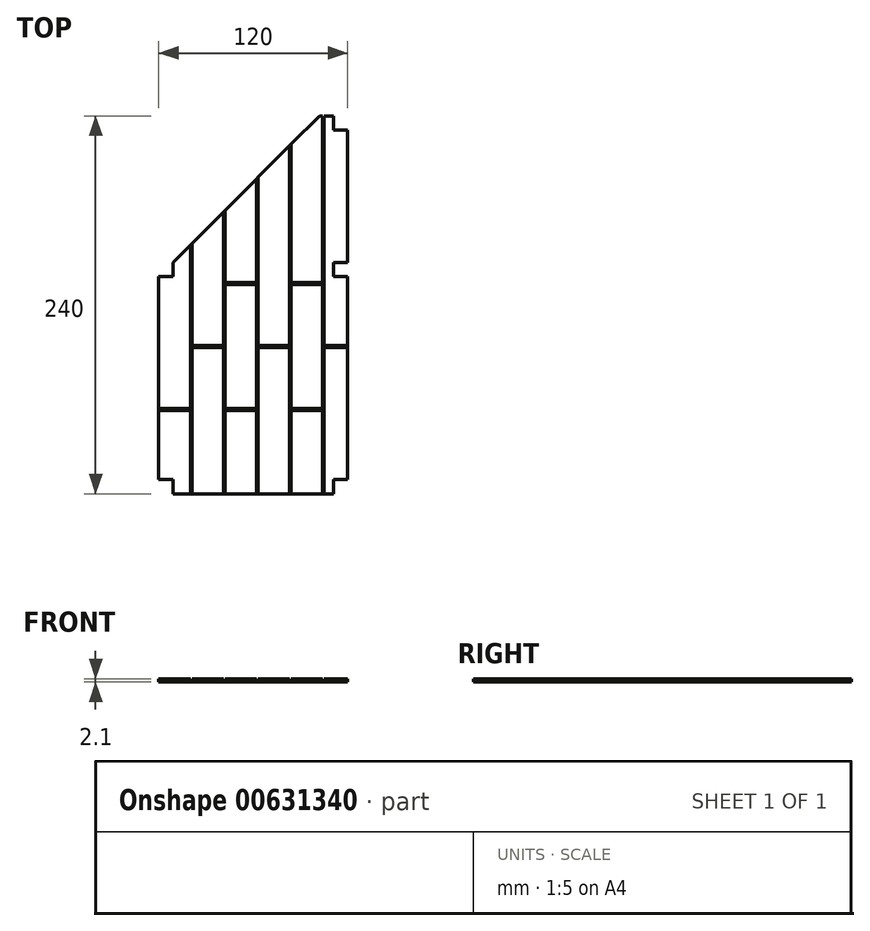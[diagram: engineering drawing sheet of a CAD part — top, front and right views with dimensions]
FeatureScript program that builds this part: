
annotation { "Feature Type Name" : "Feature", "Feature Type Description" : "" }
export const myFeature = defineFeature(function(context is Context, id is Id, definition is map)
    precondition{}
    {
        {
            var Q0;
            Q0=qCreatedBy(makeId("Top.planeOp"),FACE);
            var sketch = newSketch(context, id + "F0", { "sketchPlane" : qUnion([Q0])});
            skLineSegment(sketch, "E0.bottom", {"start": v(-143.47, 246.7) * mm, "end": v(-23.47, 246.7) * mm});
            skLineSegment(sketch, "E0.top", {"start": v(-143.47, 6.7) * mm, "end": v(-23.47, 6.7) * mm});
            skLineSegment(sketch, "E0.left", {"start": v(-143.47, 246.7) * mm, "end": v(-143.47, 6.7) * mm});
            skLineSegment(sketch, "E0.right", {"start": v(-23.47, 246.7) * mm, "end": v(-23.47, 6.7) * mm});
            skLineSegment(sketch, "E1.bottom", {"start": v(-143.47, 153.7) * mm, "end": v(-134.47, 153.7) * mm});
            skLineSegment(sketch, "E1.top", {"start": v(-143.47, 144.7) * mm, "end": v(-134.47, 144.7) * mm});
            skLineSegment(sketch, "E1.left", {"start": v(-143.47, 153.7) * mm, "end": v(-143.47, 144.7) * mm});
            skLineSegment(sketch, "E1.right", {"start": v(-134.47, 153.7) * mm, "end": v(-134.47, 144.7) * mm});
            skLineSegment(sketch, "E2.bottom", {"start": v(-134.47, 6.7) * mm, "end": v(-143.47, 6.7) * mm});
            skLineSegment(sketch, "E2.top", {"start": v(-134.47, 15.7) * mm, "end": v(-143.47, 15.7) * mm});
            skLineSegment(sketch, "E2.left", {"start": v(-134.47, 6.7) * mm, "end": v(-134.47, 15.7) * mm});
            skLineSegment(sketch, "E2.right", {"start": v(-143.47, 6.7) * mm, "end": v(-143.47, 15.7) * mm});
            skLineSegment(sketch, "E3.bottom", {"start": v(-23.47, 15.7) * mm, "end": v(-32.47, 15.7) * mm});
            skLineSegment(sketch, "E3.top", {"start": v(-23.47, 6.7) * mm, "end": v(-32.47, 6.7) * mm});
            skLineSegment(sketch, "E3.left", {"start": v(-23.47, 15.7) * mm, "end": v(-23.47, 6.7) * mm});
            skLineSegment(sketch, "E3.right", {"start": v(-32.47, 15.7) * mm, "end": v(-32.47, 6.7) * mm});
            skLineSegment(sketch, "E4.bottom", {"start": v(-23.47, 153.7) * mm, "end": v(-32.47, 153.7) * mm});
            skLineSegment(sketch, "E4.top", {"start": v(-23.47, 144.7) * mm, "end": v(-32.47, 144.7) * mm});
            skLineSegment(sketch, "E4.left", {"start": v(-23.47, 153.7) * mm, "end": v(-23.47, 144.7) * mm});
            skLineSegment(sketch, "E4.right", {"start": v(-32.47, 153.7) * mm, "end": v(-32.47, 144.7) * mm});
            skLineSegment(sketch, "E5.bottom", {"start": v(-23.47, 246.7) * mm, "end": v(-32.47, 246.7) * mm});
            skLineSegment(sketch, "E5.top", {"start": v(-23.47, 237.7) * mm, "end": v(-32.47, 237.7) * mm});
            skLineSegment(sketch, "E5.left", {"start": v(-23.47, 246.7) * mm, "end": v(-23.47, 237.7) * mm});
            skLineSegment(sketch, "E5.right", {"start": v(-32.47, 246.7) * mm, "end": v(-32.47, 237.7) * mm});
            skLineSegment(sketch, "E6.bottom", {"start": v(-32.47, 246.7) * mm, "end": v(-41.47, 246.7) * mm});
            skLineSegment(sketch, "E6.top", {"start": v(-32.47, 237.7) * mm, "end": v(-41.47, 237.7) * mm});
            skLineSegment(sketch, "E6.right", {"start": v(-41.47, 246.7) * mm, "end": v(-41.47, 237.7) * mm});
            skLineSegment(sketch, "E7", {"start": v(-41.47, 246.7) * mm, "end": v(-134.47, 153.7) * mm});
            skLineSegment(sketch, "E8", {"start": v(-123.47, 6.7) * mm, "end": v(-123.47, 164.7) * mm});
            skLineSegment(sketch, "E9", {"start": v(-122.47, 6.7) * mm, "end": v(-122.47, 165.7) * mm});
            skLineSegment(sketch, "E10", {"start": v(-102.47, 6.7) * mm, "end": v(-102.47, 185.7) * mm});
            skLineSegment(sketch, "E11", {"start": v(-101.47, 6.7) * mm, "end": v(-101.47, 186.7) * mm});
            skLineSegment(sketch, "E12", {"start": v(-81.47, 6.7) * mm, "end": v(-81.47, 206.7) * mm});
            skLineSegment(sketch, "E13", {"start": v(-80.47, 6.7) * mm, "end": v(-80.47, 207.7) * mm});
            skLineSegment(sketch, "E14", {"start": v(-60.47, 6.7) * mm, "end": v(-60.47, 227.7) * mm});
            skLineSegment(sketch, "E15", {"start": v(-59.47, 6.7) * mm, "end": v(-59.47, 228.7) * mm});
            skLineSegment(sketch, "E16", {"start": v(-39.47, 6.7) * mm, "end": v(-39.47, 246.7) * mm});
            skLineSegment(sketch, "E17", {"start": v(-143.47, 60.7) * mm, "end": v(-123.47, 60.7) * mm});
            skLineSegment(sketch, "E18", {"start": v(-143.47, 59.7) * mm, "end": v(-123.47, 59.7) * mm});
            skLineSegment(sketch, "E19", {"start": v(-122.47, 100.7) * mm, "end": v(-102.47, 100.7) * mm});
            skLineSegment(sketch, "E20", {"start": v(-122.47, 99.7) * mm, "end": v(-102.47, 99.7) * mm});
            skLineSegment(sketch, "E21.bottom", {"start": v(-143.47, 64.7) * mm, "end": v(-152.47, 64.7) * mm});
            skLineSegment(sketch, "E21.top", {"start": v(-143.47, 55.7) * mm, "end": v(-152.47, 55.7) * mm});
            skLineSegment(sketch, "E21.left", {"start": v(-143.47, 64.7) * mm, "end": v(-143.47, 55.7) * mm});
            skLineSegment(sketch, "E21.right", {"start": v(-152.47, 64.7) * mm, "end": v(-152.47, 55.7) * mm});
            skLineSegment(sketch, "E22.bottom", {"start": v(-143.47, 104.7) * mm, "end": v(-152.47, 104.7) * mm});
            skLineSegment(sketch, "E22.top", {"start": v(-143.47, 95.7) * mm, "end": v(-152.47, 95.7) * mm});
            skLineSegment(sketch, "E22.left", {"start": v(-143.47, 104.7) * mm, "end": v(-143.47, 95.7) * mm});
            skLineSegment(sketch, "E22.right", {"start": v(-152.47, 104.7) * mm, "end": v(-152.47, 95.7) * mm});
            skLineSegment(sketch, "E23", {"start": v(-101.47, 140.7) * mm, "end": v(-81.47, 140.7) * mm});
            skPoint(sketch, "E23.startSnap0", {"position": v(-134.47, 149.2) * mm});
            skLineSegment(sketch, "E24", {"start": v(-101.47, 139.7) * mm, "end": v(-81.47, 139.7) * mm});
            skLineSegment(sketch, "E25", {"start": v(-101.47, 60.7) * mm, "end": v(-81.47, 60.7) * mm});
            skLineSegment(sketch, "E26", {"start": v(-101.47, 59.7) * mm, "end": v(-81.47, 59.7) * mm});
            skLineSegment(sketch, "E27", {"start": v(-80.47, 100.7) * mm, "end": v(-60.47, 100.7) * mm});
            skLineSegment(sketch, "E28", {"start": v(-80.47, 99.7) * mm, "end": v(-60.47, 99.7) * mm});
            skLineSegment(sketch, "E29", {"start": v(-59.47, 140.7) * mm, "end": v(-39.47, 140.7) * mm});
            skLineSegment(sketch, "E30", {"start": v(-59.47, 139.7) * mm, "end": v(-39.47, 139.7) * mm});
            skLineSegment(sketch, "E31", {"start": v(-59.47, 60.7) * mm, "end": v(-39.47, 60.7) * mm});
            skLineSegment(sketch, "E32", {"start": v(-59.47, 59.7) * mm, "end": v(-39.47, 59.7) * mm});
            skLineSegment(sketch, "E33", {"start": v(-38.47, 246.7) * mm, "end": v(-38.47, 6.7) * mm});
            skLineSegment(sketch, "E34", {"start": v(-38.47, 100.7) * mm, "end": v(-23.47, 100.7) * mm});
            skLineSegment(sketch, "E35", {"start": v(-38.47, 99.7) * mm, "end": v(-23.47, 99.7) * mm});
            skSolve(sketch);
        }
        {
            var Q0;
            {var subQ4=sQuery(id+"F0.wireOp",EDGE,"E1.top");Q0=makeQuery(id+"F0.imprint","IMPRINT",FACE,{"disambiguationData":[TD([[makeQuery(id+"F0.imprint","IMPRINT",EDGE,{"derivedFrom":subQ4}),-1.0]])]});}
            var Q1;
            {var subQ0=sQuery(id+"F0.wireOp",EDGE,"iPl3nyO9-lugT-xWKg-2Qvq-ciyDfMvkzASw");Q1=makeQuery(id+"F0.imprint","IMPRINT",FACE,{"disambiguationData":[TD([[makeQuery(id+"F0.imprint","IMPRINT",EDGE,{"derivedFrom":subQ0}),-1.0]])]});}
            var Q2;
            {var subQ1=sQuery(id+"F0.wireOp",EDGE,"E2.top");Q2=makeQuery(id+"F0.imprint","IMPRINT",FACE,{"disambiguationData":[TD([[makeQuery(id+"F0.imprint","IMPRINT",EDGE,{"derivedFrom":subQ1}),-1.0]])]});}
            var Q3;
            {var subQ5=sQuery(id+"F0.wireOp",EDGE,"E20");Q3=makeQuery(id+"F0.imprint","IMPRINT",FACE,{"disambiguationData":[TD([[makeQuery(id+"F0.imprint","IMPRINT",EDGE,{"derivedFrom":subQ5}),-1.0]])]});}
            var Q4;
            {var subQ5=sQuery(id+"F0.wireOp",EDGE,"E19");Q4=makeQuery(id+"F0.imprint","IMPRINT",FACE,{"disambiguationData":[TD([[makeQuery(id+"F0.imprint","IMPRINT",EDGE,{"derivedFrom":subQ5}),1.0]])]});}
            var Q5;
            {var subQ5=sQuery(id+"F0.wireOp",EDGE,"E23");Q5=makeQuery(id+"F0.imprint","IMPRINT",FACE,{"disambiguationData":[TD([[makeQuery(id+"F0.imprint","IMPRINT",EDGE,{"derivedFrom":subQ5}),1.0]])]});}
            var Q6;
            {var subQ0=sQuery(id+"F0.wireOp",EDGE,"E24");Q6=makeQuery(id+"F0.imprint","IMPRINT",FACE,{"disambiguationData":[TD([[makeQuery(id+"F0.imprint","IMPRINT",EDGE,{"derivedFrom":subQ0}),-1.0]])]});}
            var Q7;
            {var subQ5=sQuery(id+"F0.wireOp",EDGE,"E26");Q7=makeQuery(id+"F0.imprint","IMPRINT",FACE,{"disambiguationData":[TD([[makeQuery(id+"F0.imprint","IMPRINT",EDGE,{"derivedFrom":subQ5}),-1.0]])]});}
            var Q8;
            {var subQ5=sQuery(id+"F0.wireOp",EDGE,"E27");Q8=makeQuery(id+"F0.imprint","IMPRINT",FACE,{"disambiguationData":[TD([[makeQuery(id+"F0.imprint","IMPRINT",EDGE,{"derivedFrom":subQ5}),1.0]])]});}
            var Q9;
            {var subQ5=sQuery(id+"F0.wireOp",EDGE,"E28");Q9=makeQuery(id+"F0.imprint","IMPRINT",FACE,{"disambiguationData":[TD([[makeQuery(id+"F0.imprint","IMPRINT",EDGE,{"derivedFrom":subQ5}),-1.0]])]});}
            var Q10;
            {var subQ4=sQuery(id+"F0.wireOp",EDGE,"E6.right");Q10=makeQuery(id+"F0.imprint","IMPRINT",FACE,{"disambiguationData":[TD([[makeQuery(id+"F0.imprint","IMPRINT",EDGE,{"derivedFrom":subQ4}),-1.0]])]});}
            var Q11;
            {var subQ0=sQuery(id+"F0.wireOp",EDGE,"E30");Q11=makeQuery(id+"F0.imprint","IMPRINT",FACE,{"disambiguationData":[TD([[makeQuery(id+"F0.imprint","IMPRINT",EDGE,{"derivedFrom":subQ0}),-1.0]])]});}
            var Q12;
            {var subQ5=sQuery(id+"F0.wireOp",EDGE,"E32");Q12=makeQuery(id+"F0.imprint","IMPRINT",FACE,{"disambiguationData":[TD([[makeQuery(id+"F0.imprint","IMPRINT",EDGE,{"derivedFrom":subQ5}),-1.0]])]});}
            var Q13;
            {var subQ0=sQuery(id+"F0.wireOp",EDGE,"E17");Q13=makeQuery(id+"F0.imprint","IMPRINT",FACE,{"disambiguationData":[TD([[makeQuery(id+"F0.imprint","IMPRINT",EDGE,{"derivedFrom":subQ0}),-1.0]])]});}
            var Q14;
            {var subQ0=sQuery(id+"F0.wireOp",EDGE,"E8");var subQ3=sQuery(id+"F0.wireOp",EDGE,"E0.top");var subQ4=makeQuery(id+"F0.imprint","INTERSECT",VERTEX,{"derivedFrom":[subQ3,subQ0]});Q14=makeQuery(id+"F0.imprint","IMPRINT",FACE,{"disambiguationData":[TD([[makeQuery(id+"F0.imprint","IMPRINT",EDGE,{"disambiguationData":[TD([[subQ4,-1.0]])],"derivedFrom":subQ3}),1.0]])]});}
            var Q15;
            {var subQ0=sQuery(id+"F0.wireOp",EDGE,"E19");Q15=makeQuery(id+"F0.imprint","IMPRINT",FACE,{"disambiguationData":[TD([[makeQuery(id+"F0.imprint","IMPRINT",EDGE,{"derivedFrom":subQ0}),-1.0]])]});}
            var Q16;
            {var subQ0=sQuery(id+"F0.wireOp",EDGE,"E10");var subQ7=sQuery(id+"F0.wireOp",EDGE,"E0.top");var subQ8=makeQuery(id+"F0.imprint","INTERSECT",VERTEX,{"derivedFrom":[subQ7,subQ0]});Q16=makeQuery(id+"F0.imprint","IMPRINT",FACE,{"disambiguationData":[TD([[makeQuery(id+"F0.imprint","IMPRINT",EDGE,{"disambiguationData":[TD([[subQ8,-1.0]])],"derivedFrom":subQ7}),1.0]])]});}
            var Q17;
            {var subQ0=sQuery(id+"F0.wireOp",EDGE,"E23");Q17=makeQuery(id+"F0.imprint","IMPRINT",FACE,{"disambiguationData":[TD([[makeQuery(id+"F0.imprint","IMPRINT",EDGE,{"derivedFrom":subQ0}),-1.0]])]});}
            var Q18;
            {var subQ0=sQuery(id+"F0.wireOp",EDGE,"E12");var subQ3=sQuery(id+"F0.wireOp",EDGE,"E0.top");var subQ4=makeQuery(id+"F0.imprint","INTERSECT",VERTEX,{"derivedFrom":[subQ3,subQ0]});Q18=makeQuery(id+"F0.imprint","IMPRINT",FACE,{"disambiguationData":[TD([[makeQuery(id+"F0.imprint","IMPRINT",EDGE,{"disambiguationData":[TD([[subQ4,-1.0]])],"derivedFrom":subQ3}),1.0]])]});}
            var Q19;
            {var subQ0=sQuery(id+"F0.wireOp",EDGE,"E27");Q19=makeQuery(id+"F0.imprint","IMPRINT",FACE,{"disambiguationData":[TD([[makeQuery(id+"F0.imprint","IMPRINT",EDGE,{"derivedFrom":subQ0}),-1.0]])]});}
            var Q20;
            {var subQ0=sQuery(id+"F0.wireOp",EDGE,"E14");var subQ1=sQuery(id+"F0.wireOp",EDGE,"E0.top");var subQ2=makeQuery(id+"F0.imprint","INTERSECT",VERTEX,{"derivedFrom":[subQ1,subQ0]});Q20=makeQuery(id+"F0.imprint","IMPRINT",FACE,{"disambiguationData":[TD([[makeQuery(id+"F0.imprint","IMPRINT",EDGE,{"disambiguationData":[TD([[subQ2,-1.0]])],"derivedFrom":subQ1}),1.0]])]});}
            var Q21;
            {var subQ0=sQuery(id+"F0.wireOp",EDGE,"E31");Q21=makeQuery(id+"F0.imprint","IMPRINT",FACE,{"disambiguationData":[TD([[makeQuery(id+"F0.imprint","IMPRINT",EDGE,{"derivedFrom":subQ0}),-1.0]])]});}
            var Q22;
            {var subQ0=sQuery(id+"F0.wireOp",EDGE,"E29");Q22=makeQuery(id+"F0.imprint","IMPRINT",FACE,{"disambiguationData":[TD([[makeQuery(id+"F0.imprint","IMPRINT",EDGE,{"derivedFrom":subQ0}),-1.0]])]});}
            var Q23;
            {var subQ0=sQuery(id+"F0.wireOp",EDGE,"E25");Q23=makeQuery(id+"F0.imprint","IMPRINT",FACE,{"disambiguationData":[TD([[makeQuery(id+"F0.imprint","IMPRINT",EDGE,{"derivedFrom":subQ0}),-1.0]])]});}
            var Q24;
            {var subQ5=sQuery(id+"F0.wireOp",EDGE,"E33");Q24=makeQuery(id+"F0.imprint","IMPRINT",FACE,{"disambiguationData":[TD([[makeQuery(id+"F0.imprint","IMPRINT",EDGE,{"derivedFrom":subQ5}),-1.0]])]});}
            var Q25;
            {var subQ9=sQuery(id+"F0.wireOp",EDGE,"E3.bottom");Q25=makeQuery(id+"F0.imprint","IMPRINT",FACE,{"disambiguationData":[TD([[makeQuery(id+"F0.imprint","IMPRINT",EDGE,{"derivedFrom":subQ9}),-1.0]])]});}
            var Q26;
            {var subQ1=sQuery(id+"F0.wireOp",EDGE,"E4.bottom");Q26=makeQuery(id+"F0.imprint","IMPRINT",FACE,{"disambiguationData":[TD([[makeQuery(id+"F0.imprint","IMPRINT",EDGE,{"derivedFrom":subQ1}),-1.0]])]});}
            var Q27;
            {var subQ0=sQuery(id+"F0.wireOp",EDGE,"E34");Q27=makeQuery(id+"F0.imprint","IMPRINT",FACE,{"disambiguationData":[TD([[makeQuery(id+"F0.imprint","IMPRINT",EDGE,{"derivedFrom":subQ0}),-1.0]])]});}
            var Q28;
            {var subQ0=sQuery(id+"F0.wireOp",EDGE,"E6.right");Q28=makeQuery(id+"F0.imprint","IMPRINT",FACE,{"disambiguationData":[TD([[makeQuery(id+"F0.imprint","IMPRINT",EDGE,{"derivedFrom":subQ0}),1.0]])]});}
            var Q29;
            {var subQ0=sQuery(id+"F0.wireOp",EDGE,"E16");var subQ1=sQuery(id+"F0.wireOp",EDGE,"E6.bottom");var subQ2=makeQuery(id+"F0.imprint","INTERSECT",VERTEX,{"derivedFrom":[subQ1,subQ0]});Q29=makeQuery(id+"F0.imprint","IMPRINT",FACE,{"disambiguationData":[TD([[makeQuery(id+"F0.imprint","IMPRINT",EDGE,{"disambiguationData":[TD([[subQ2,1.0]])],"derivedFrom":subQ1}),1.0]])]});}
            var Q30;
            {var subQ0=sQuery(id+"F0.wireOp",EDGE,"E5.right");Q30=makeQuery(id+"F0.imprint","IMPRINT",FACE,{"disambiguationData":[TD([[makeQuery(id+"F0.imprint","IMPRINT",EDGE,{"derivedFrom":subQ0}),-1.0]])]});}
            extrude(context, id + "F1", {"entities" : qUnion([Q0, Q1, Q2, Q3, Q4, Q5, Q6, Q7, Q8, Q9, Q10, Q11, Q12, Q13, Q14, Q15, Q16, Q17, Q18, Q19, Q20, Q21, Q22, Q23, Q24, Q25, Q26, Q27, Q28, Q29, Q30]), "depth" : -0.1 * mm, "offsetDistance" : 25 * mm});
        }
        {
            var Q0;
            {var subQ2=sQuery(id+"F0.wireOp",EDGE,"E1.top");Q0=makeQuery(id+"F0.imprint","IMPRINT",FACE,{"disambiguationData":[TD([[makeQuery(id+"F0.imprint","IMPRINT",EDGE,{"derivedFrom":subQ2}),-1.0]])]});}
            var Q1;
            {var subQ4=sQuery(id+"F0.wireOp",EDGE,"E2.top");Q1=makeQuery(id+"F0.imprint","IMPRINT",FACE,{"disambiguationData":[TD([[makeQuery(id+"F0.imprint","IMPRINT",EDGE,{"derivedFrom":subQ4}),-1.0]])]});}
            var Q2;
            {var subQ5=sQuery(id+"F0.wireOp",EDGE,"E20");Q2=makeQuery(id+"F0.imprint","IMPRINT",FACE,{"disambiguationData":[TD([[makeQuery(id+"F0.imprint","IMPRINT",EDGE,{"derivedFrom":subQ5}),-1.0]])]});}
            var Q3;
            {var subQ5=sQuery(id+"F0.wireOp",EDGE,"E19");Q3=makeQuery(id+"F0.imprint","IMPRINT",FACE,{"disambiguationData":[TD([[makeQuery(id+"F0.imprint","IMPRINT",EDGE,{"derivedFrom":subQ5}),1.0]])]});}
            var Q4;
            {var subQ5=sQuery(id+"F0.wireOp",EDGE,"E23");Q4=makeQuery(id+"F0.imprint","IMPRINT",FACE,{"disambiguationData":[TD([[makeQuery(id+"F0.imprint","IMPRINT",EDGE,{"derivedFrom":subQ5}),1.0]])]});}
            var Q5;
            {var subQ0=sQuery(id+"F0.wireOp",EDGE,"E24");Q5=makeQuery(id+"F0.imprint","IMPRINT",FACE,{"disambiguationData":[TD([[makeQuery(id+"F0.imprint","IMPRINT",EDGE,{"derivedFrom":subQ0}),-1.0]])]});}
            var Q6;
            {var subQ5=sQuery(id+"F0.wireOp",EDGE,"E26");Q6=makeQuery(id+"F0.imprint","IMPRINT",FACE,{"disambiguationData":[TD([[makeQuery(id+"F0.imprint","IMPRINT",EDGE,{"derivedFrom":subQ5}),-1.0]])]});}
            var Q7;
            {var subQ5=sQuery(id+"F0.wireOp",EDGE,"E28");Q7=makeQuery(id+"F0.imprint","IMPRINT",FACE,{"disambiguationData":[TD([[makeQuery(id+"F0.imprint","IMPRINT",EDGE,{"derivedFrom":subQ5}),-1.0]])]});}
            var Q8;
            {var subQ5=sQuery(id+"F0.wireOp",EDGE,"E27");Q8=makeQuery(id+"F0.imprint","IMPRINT",FACE,{"disambiguationData":[TD([[makeQuery(id+"F0.imprint","IMPRINT",EDGE,{"derivedFrom":subQ5}),1.0]])]});}
            var Q9;
            {var subQ4=sQuery(id+"F0.wireOp",EDGE,"E6.right");Q9=makeQuery(id+"F0.imprint","IMPRINT",FACE,{"disambiguationData":[TD([[makeQuery(id+"F0.imprint","IMPRINT",EDGE,{"derivedFrom":subQ4}),-1.0]])]});}
            var Q10;
            {var subQ0=sQuery(id+"F0.wireOp",EDGE,"E30");Q10=makeQuery(id+"F0.imprint","IMPRINT",FACE,{"disambiguationData":[TD([[makeQuery(id+"F0.imprint","IMPRINT",EDGE,{"derivedFrom":subQ0}),-1.0]])]});}
            var Q11;
            {var subQ5=sQuery(id+"F0.wireOp",EDGE,"E32");Q11=makeQuery(id+"F0.imprint","IMPRINT",FACE,{"disambiguationData":[TD([[makeQuery(id+"F0.imprint","IMPRINT",EDGE,{"derivedFrom":subQ5}),-1.0]])]});}
            var Q12;
            {var subQ9=sQuery(id+"F0.wireOp",EDGE,"E3.bottom");Q12=makeQuery(id+"F0.imprint","IMPRINT",FACE,{"disambiguationData":[TD([[makeQuery(id+"F0.imprint","IMPRINT",EDGE,{"derivedFrom":subQ9}),-1.0]])]});}
            var Q13;
            {var subQ1=sQuery(id+"F0.wireOp",EDGE,"E4.bottom");Q13=makeQuery(id+"F0.imprint","IMPRINT",FACE,{"disambiguationData":[TD([[makeQuery(id+"F0.imprint","IMPRINT",EDGE,{"derivedFrom":subQ1}),-1.0]])]});}
            var Q14;
            {var subQ0=sQuery(id+"F0.wireOp",EDGE,"E6.right");Q14=makeQuery(id+"F0.imprint","IMPRINT",FACE,{"disambiguationData":[TD([[makeQuery(id+"F0.imprint","IMPRINT",EDGE,{"derivedFrom":subQ0}),1.0]])]});}
            var Q15;
            {var subQ0=sQuery(id+"F0.wireOp",EDGE,"E5.right");Q15=makeQuery(id+"F0.imprint","IMPRINT",FACE,{"disambiguationData":[TD([[makeQuery(id+"F0.imprint","IMPRINT",EDGE,{"derivedFrom":subQ0}),-1.0]])]});}
            extrude(context, id + "F2", {"entities" : qUnion([Q0, Q1, Q2, Q3, Q4, Q5, Q6, Q7, Q8, Q9, Q10, Q11, Q12, Q13, Q14, Q15]), "operationType" : NewBodyOperationType.ADD, "depth" : 2 * mm, "offsetDistance" : 25 * mm});
        }
    });
